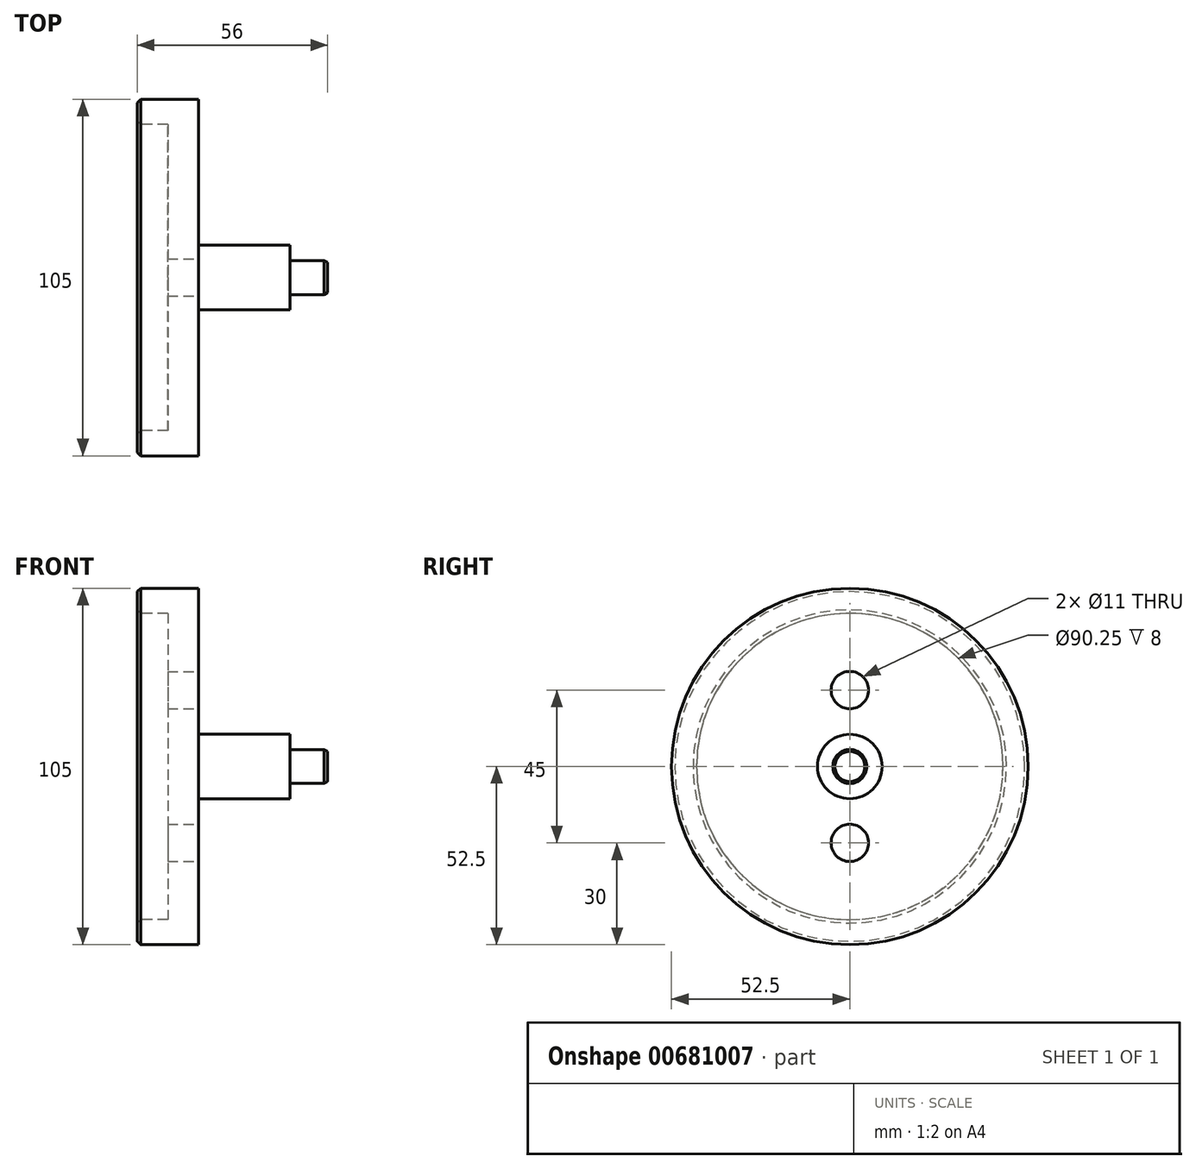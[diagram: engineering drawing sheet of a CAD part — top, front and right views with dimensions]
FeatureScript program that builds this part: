
annotation { "Feature Type Name" : "Feature", "Feature Type Description" : "" }
export const myFeature = defineFeature(function(context is Context, id is Id, definition is map)
    precondition{}
    {
        {
            var Q0;
            Q0=qCreatedBy(makeId("Right.planeOp"),FACE);
            var sketch = newSketch(context, id + "F0", { "sketchPlane" : qUnion([Q0])});
            skCircle(sketch, "E0", {"center": v(0, 0) * mm, "radius": 52.5 * mm});
            skSolve(sketch);
        }
        {
            var Q0;
            Q0=qSketchRegion(id+"F0",true);
            extrude(context, id + "F1", {"entities" : qUnion([Q0]), "oppositeDirection" : true, "depth" : (56 - 38) * mm, "offsetDistance" : 25 * mm});
        }
        {
            var Q0;
            Q0=makeQuery(id+"F1.opExtrude","CAP_FACE",FACE,{"disambiguationData":[OSD([sQuery(id+"F0.wireOp",EDGE,"E0")])],"isStart":false});
            var sketch = newSketch(context, id + "F2", { "sketchPlane" : qUnion([Q0])});
            skCircle(sketch, "E1", {"center": v(0, 0) * mm, "radius": 45.12 * mm});
            skSolve(sketch);
        }
        {
            var Q0;
            Q0=qSketchRegion(id+"F2",true);
            extrude(context, id + "F3", {"entities" : qUnion([Q0]), "operationType" : NewBodyOperationType.REMOVE, "oppositeDirection" : true, "depth" : 9 * mm, "offsetDistance" : 25 * mm});
        }
        {
            var Q0;
            Q0=makeQuery(id+"F1.opExtrude","CAP_FACE",FACE,{"disambiguationData":[OSD([sQuery(id+"F0.wireOp",EDGE,"E0")])],"isStart":false});
            chamfer(context, id + "F4", {"entities" : qUnion([Q0]), "width" : 1 * mm, "tangentPropagation" : true});
        }
        {
            var Q0;
            Q0=makeQuery(id+"F1.opExtrude","CAP_FACE",FACE,{"disambiguationData":[OSD([sQuery(id+"F0.wireOp",EDGE,"E0")])],"isStart":true});
            var sketch = newSketch(context, id + "F5", { "sketchPlane" : qUnion([Q0])});
            skCircle(sketch, "E2", {"center": v(0, 0) * mm, "radius": 9.5 * mm});
            skSolve(sketch);
        }
        {
            var Q0;
            Q0=qSketchRegion(id+"F5",true);
            extrude(context, id + "F6", {"entities" : qUnion([Q0]), "operationType" : NewBodyOperationType.ADD, "depth" : (38 - 11) * mm, "offsetDistance" : 25 * mm});
        }
        {
            var Q0;
            Q0=makeQuery(id+"F6.opExtrude","CAP_FACE",FACE,{"disambiguationData":[OSD([sQuery(id+"F5.wireOp",EDGE,"E2")])],"isStart":false});
            var sketch = newSketch(context, id + "F7", { "sketchPlane" : qUnion([Q0])});
            skCircle(sketch, "E3", {"center": v(0, 0) * mm, "radius": 5 * mm});
            skSolve(sketch);
        }
        {
            var Q0;
            Q0=qSketchRegion(id+"F7",true);
            extrude(context, id + "F8", {"entities" : qUnion([Q0]), "operationType" : NewBodyOperationType.ADD, "depth" : 11 * mm, "offsetDistance" : 25 * mm});
        }
        {
            var Q0;
            Q0=makeQuery(id+"F8.opExtrude","CAP_EDGE",EDGE,{"disambiguationData":[OSD([sQuery(id+"F7.wireOp",EDGE,"E3")])],"isStart":false});
            chamfer(context, id + "F9", {"entities" : qUnion([Q0]), "chamferType" : ChamferType.OFFSET_ANGLE, "width" : 1 * mm, "oppositeDirection" : true, "angle" : 30 * degree, "tangentPropagation" : true});
        }
        {
            var Q0;
            Q0=makeQuery(id+"F1.opExtrude","CAP_FACE",FACE,{"disambiguationData":[OSD([sQuery(id+"F0.wireOp",EDGE,"E0")])],"isStart":true});
            var sketch = newSketch(context, id + "F10", { "sketchPlane" : qUnion([Q0])});
            skLineSegment(sketch, "E4", {"start": v(0, -22.5) * mm, "end": v(0, 22.5) * mm, "construction": true});
            skPoint(sketch, "E5", {"position": v(0, -22.5) * mm});
            skPoint(sketch, "E6", {"position": v(0, 22.5) * mm});
            skSolve(sketch);
        }
        {
            var Q0;
            Q0=sQuery(id+"F10.wireOp",VERTEX,"E5");
            var Q1;
            Q1=sQuery(id+"F10.wireOp",VERTEX,"E6");
            var Q2;
            Q2=makeQuery(id+"F1.opExtrude","SWEPT_BODY",BODY,{"disambiguationData":[OSD([sQuery(id+"F0.wireOp",EDGE,"E0")])]});
            hole(context, id + "F11", {"style" : HoleStyle.SIMPLE, "endStyle" : HoleEndStyle.THROUGH, "holeDiameter" : 11 * mm, "majorDiameter" : 5 * mm, "isTappedThrough" : true, "tappedDepth" : 24.75 * mm, "tapClearance" : 3, "locations" : qUnion([Q0, Q1]), "scope" : qUnion([Q2])});
        }
    });
